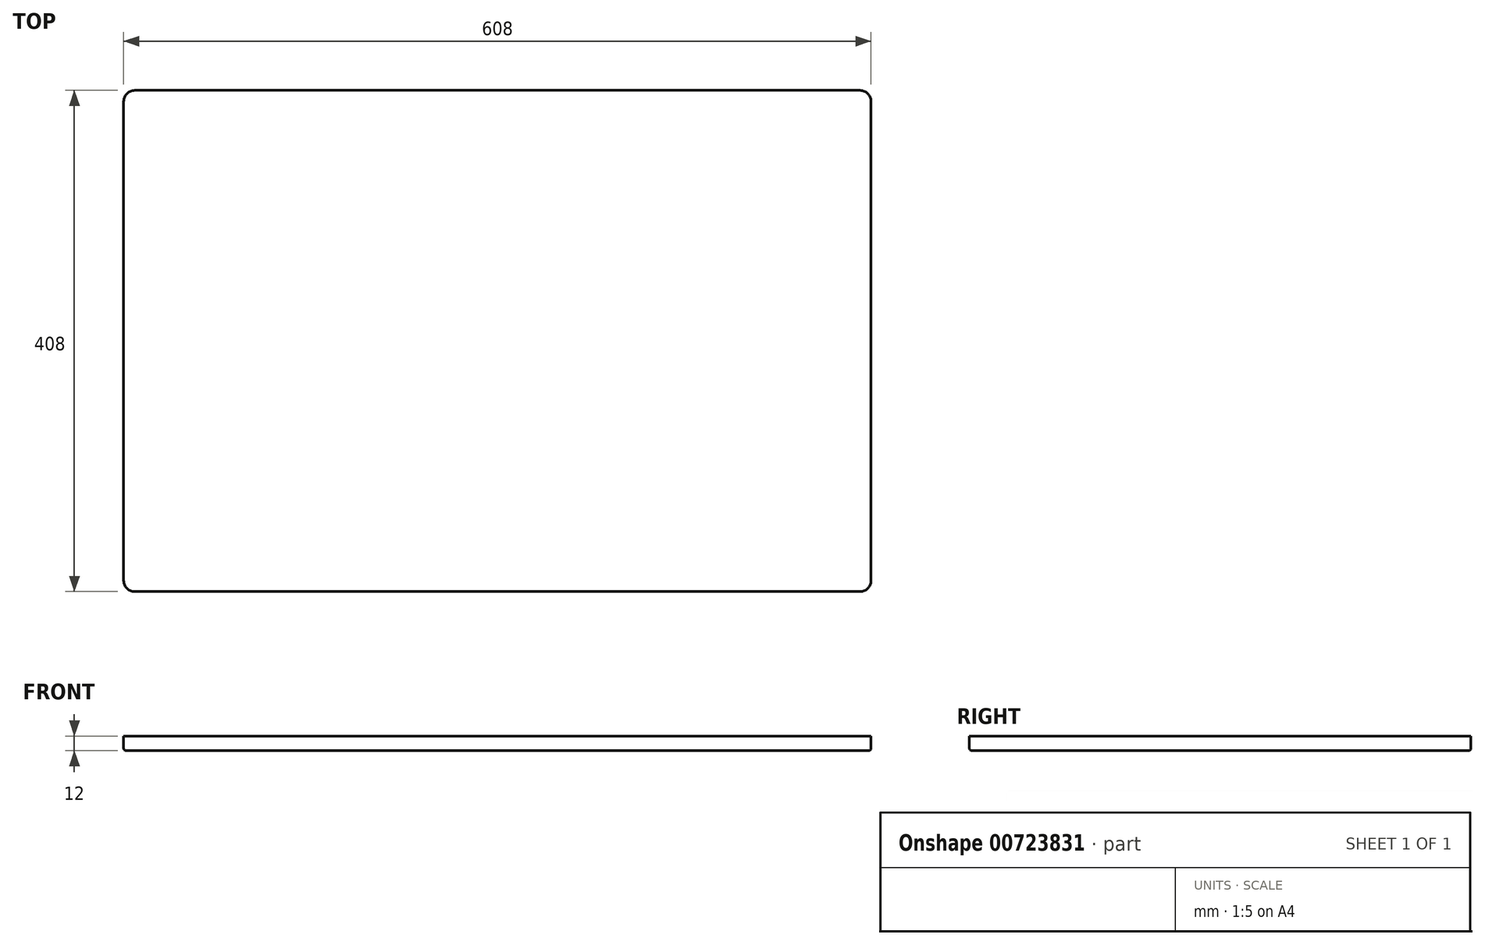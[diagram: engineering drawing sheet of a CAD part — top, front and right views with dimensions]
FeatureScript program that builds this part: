
annotation { "Feature Type Name" : "Feature", "Feature Type Description" : "" }
export const myFeature = defineFeature(function(context is Context, id is Id, definition is map)
    precondition{}
    {
        {
            var Q0;
            Q0=qCreatedBy(makeId("Top.planeOp"),FACE);
            var sketch = newSketch(context, id + "F0", { "sketchPlane" : qUnion([Q0])});
            skLineSegment(sketch, "E0.bottom", {"start": v(304, 204) * mm, "end": v(-304, 204) * mm});
            skLineSegment(sketch, "E0.top", {"start": v(304, -204) * mm, "end": v(-304, -204) * mm});
            skLineSegment(sketch, "E0.left", {"start": v(304, 204) * mm, "end": v(304, -204) * mm});
            skLineSegment(sketch, "E0.right", {"start": v(-304, 204) * mm, "end": v(-304, -204) * mm});
            skPoint(sketch, "E0.middle", {"position": v(0, 0) * mm});
            skSolve(sketch);
        }
        {
            var Q0;
            Q0=makeQuery(id+"F0.imprint","IMPRINT",FACE,{"disambiguationData":[TD([[makeQuery(id+"F0.imprint","IMPRINT",EDGE,{"derivedFrom":sQuery(id+"F0.wireOp",EDGE,"E0.bottom")}),1.0]])]});
            extrude(context, id + "F1", {"entities" : qUnion([Q0]), "depth" : 12 * mm, "offsetDistance" : 25 * mm});
        }
        {
            var Q0;
            Q0=makeQuery(id+"F1.opExtrude","SWEPT_EDGE",EDGE,{"disambiguationData":[OSD([sQuery(id+"F0.wireOp",EDGE,"E0.bottom"),sQuery(id+"F0.wireOp",EDGE,"E0.right")])]});
            var Q1;
            Q1=makeQuery(id+"F1.opExtrude","SWEPT_EDGE",EDGE,{"disambiguationData":[OSD([sQuery(id+"F0.wireOp",EDGE,"E0.top"),sQuery(id+"F0.wireOp",EDGE,"E0.right")])]});
            var Q2;
            Q2=makeQuery(id+"F1.opExtrude","SWEPT_EDGE",EDGE,{"disambiguationData":[OSD([sQuery(id+"F0.wireOp",EDGE,"E0.top"),sQuery(id+"F0.wireOp",EDGE,"E0.left")])]});
            var Q3;
            Q3=makeQuery(id+"F1.opExtrude","SWEPT_EDGE",EDGE,{"disambiguationData":[OSD([sQuery(id+"F0.wireOp",EDGE,"E0.bottom"),sQuery(id+"F0.wireOp",EDGE,"E0.left")])]});
            fillet(context, id + "F2", {"entities" : qUnion([Q0, Q1, Q2, Q3]), "radius" : 9 * mm, "tangentPropagation" : true, "allowEdgeOverflow" : false});
        }
        {
            var Q0;
            Q0=makeQuery(id+"F1.opExtrude","CAP_EDGE",EDGE,{"disambiguationData":[OSD([sQuery(id+"F0.wireOp",EDGE,"E0.top")])],"isStart":true});
            fillet(context, id + "F3", {"entities" : qUnion([Q0]), "radius" : 2 * mm, "tangentPropagation" : true, "allowEdgeOverflow" : false});
        }
    });
